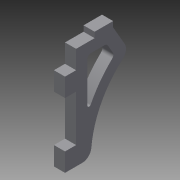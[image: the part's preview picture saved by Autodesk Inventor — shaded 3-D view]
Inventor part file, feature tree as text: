
AUTODESK INVENTOR PART (.ipt)
format: ipt  version: 2015 (Build 190159000, 159)  size: 132,608 bytes
history: native  units: mm
features: fillet x3, extrude x2, sketch x2
ambient origin geometry x8: Origin, YZ Plane, XZ Plane, XY Plane, X Axis, Y Axis, Z Axis, Center Point
bodies: Body1 (feature_tree)
feature tree (7):
  extrude  "Extrusion2"  TaperAngle=60.0deg  [1 undecoded]
  fillet  "Fillet3"  Radius=50.0mm
  extrude  "Extrusion3"  Depth=10.0mm
  fillet  "Fillet4"  Radius=10.0mm
  fillet  "Fillet5"  Radius=6.0mm
  sketch  "Sketch1"  dims[d0=100.0mm d4=60.0deg d5=60.0deg d6=50.0mm]
  sketch  "Sketch2"  dims[d8=10.0mm d9=10.0mm d10=3.0mm d11=10.0mm d12=6.0mm d13=11.145398mm d14=55.0mm d15=55.0mm d17=120.0deg d18=10.0mm d19=5.0mm d21=10.0mm d23=45.0deg d25=15.0deg d26=0.0mm d30=10.0mm d31=6.0mm d32=25.0mm d38=58.0mm d39=6.0mm d40=0.0mm d41=5.0mm d42=6.0mm d43=6.0mm d44=6.0mm d45=56.0mm d46=6.0mm d47=0.0mm d48=1.0mm d49=2.0mm]
note: 1 required parameter value undecoded (feature->parameter linkage not recoverable at this tier; creation-order binding heuristic only, values carry confidence <= 0.55)
